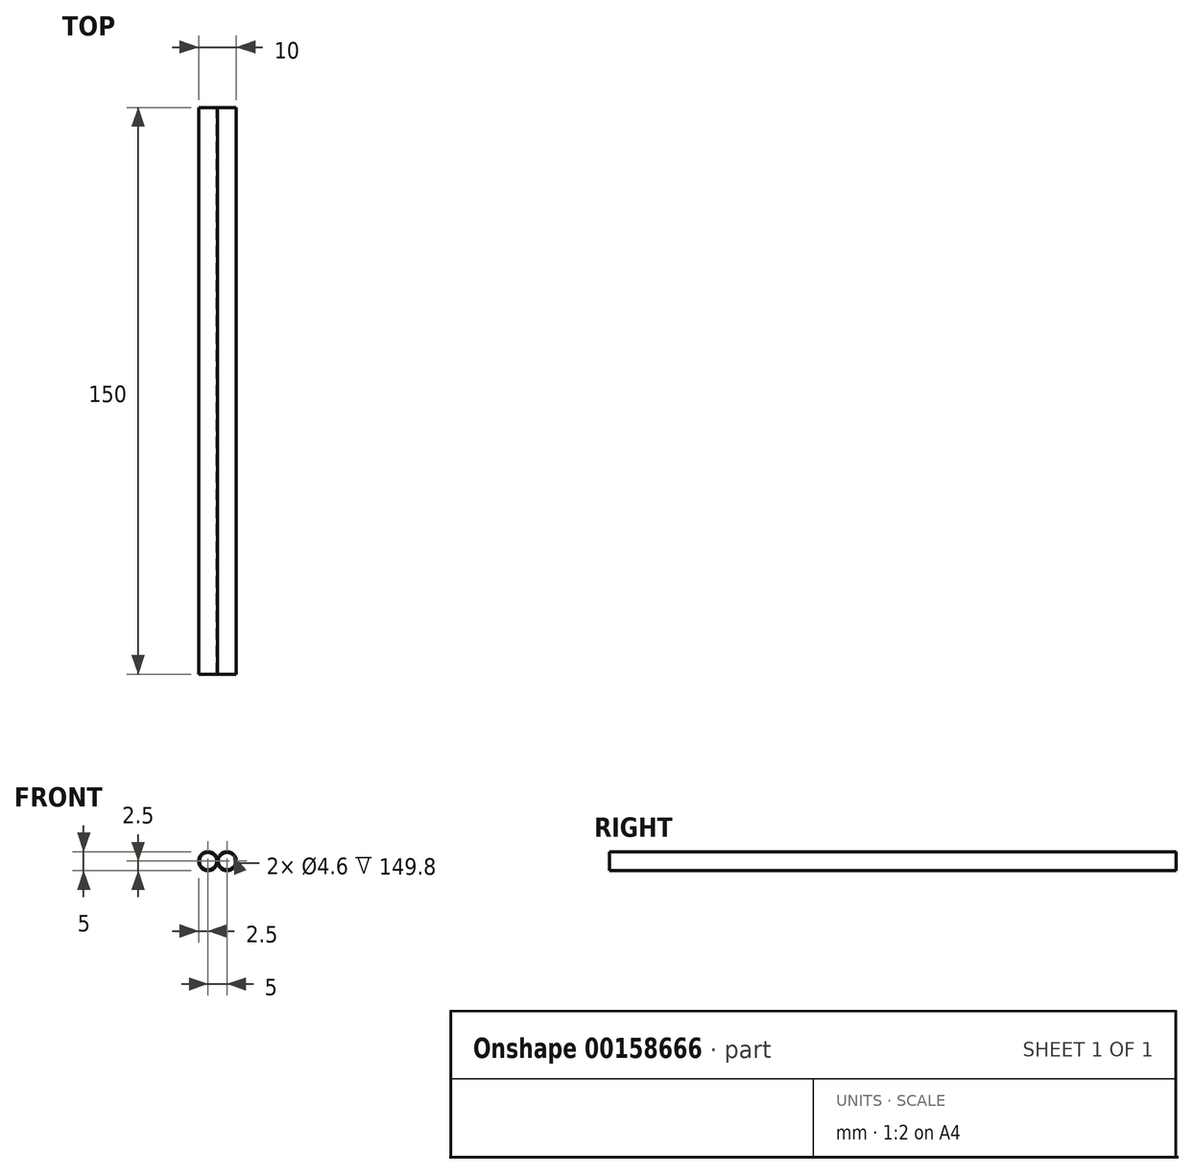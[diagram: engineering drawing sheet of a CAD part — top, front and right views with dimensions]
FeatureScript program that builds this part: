
annotation { "Feature Type Name" : "Feature", "Feature Type Description" : "" }
export const myFeature = defineFeature(function(context is Context, id is Id, definition is map)
    precondition{}
    {
        {
            var Q0;
            Q0=qCreatedBy(makeId("Front.planeOp"),FACE);
            var sketch = newSketch(context, id + "F0", { "sketchPlane" : qUnion([Q0])});
            skLineSegment(sketch, "E0", {"start": v(-2.5, 0) * mm, "end": v(2.5, 0) * mm, "construction": true});
            skCircle(sketch, "E1", {"center": v(-2.5, 0) * mm, "radius": 2.5 * mm});
            skCircle(sketch, "E2", {"center": v(2.5, 0) * mm, "radius": 2.5 * mm});
            skSolve(sketch);
        }
        {
            var Q0;
            Q0=makeQuery(id+"F0.imprint","IMPRINT",FACE,{"disambiguationData":[TD([[makeQuery(id+"F0.imprint","IMPRINT",EDGE,{"derivedFrom":sQuery(id+"F0.wireOp",EDGE,"E1")}),1.0]])]});
            var Q1;
            Q1=makeQuery(id+"F0.imprint","IMPRINT",FACE,{"disambiguationData":[TD([[makeQuery(id+"F0.imprint","IMPRINT",EDGE,{"derivedFrom":sQuery(id+"F0.wireOp",EDGE,"E2")}),1.0]])]});
            extrude(context, id + "F1", {"entities" : qUnion([Q0, Q1]), "depth" : 150 * mm});
        }
        {
            var Q0;
            Q0=makeQuery(id+"F1.opExtrude","CAP_FACE",FACE,{"disambiguationData":[OSD([sQuery(id+"F0.wireOp",EDGE,"E1")])],"isStart":false});
            var Q1;
            Q1=makeQuery(id+"F1.opExtrude","CAP_FACE",FACE,{"disambiguationData":[OSD([sQuery(id+"F0.wireOp",EDGE,"E2")])],"isStart":false});
            shell(context, id + "F2", {"entities" : qUnion([Q0, Q1]), "thickness" : 0.2 * mm});
        }
    });
